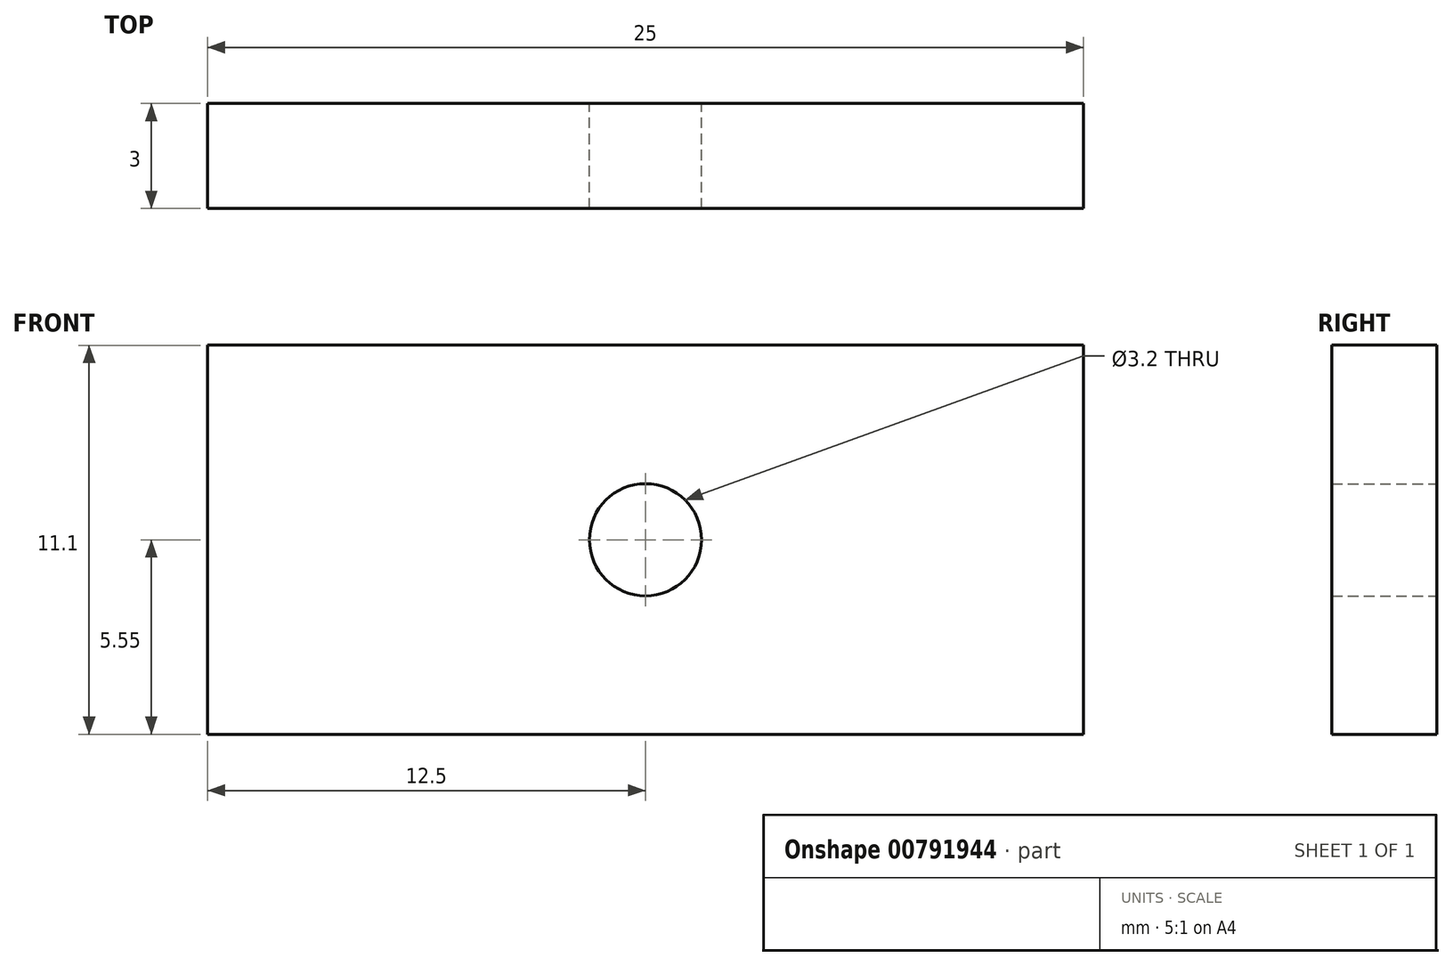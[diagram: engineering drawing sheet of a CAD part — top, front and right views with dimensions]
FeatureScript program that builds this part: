
annotation { "Feature Type Name" : "Feature", "Feature Type Description" : "" }
export const myFeature = defineFeature(function(context is Context, id is Id, definition is map)
    precondition{}
    {
        {
            var Q0;
            Q0=qCreatedBy(makeId("Front.planeOp"),FACE);
            var sketch = newSketch(context, id + "F0", { "sketchPlane" : qUnion([Q0])});
            skLineSegment(sketch, "E0.bottom", {"start": v(12.5, 5.56) * mm, "end": v(-12.5, 5.56) * mm});
            skLineSegment(sketch, "E0.top", {"start": v(12.5, -5.56) * mm, "end": v(-12.5, -5.56) * mm});
            skLineSegment(sketch, "E0.left", {"start": v(12.5, 5.56) * mm, "end": v(12.5, -5.56) * mm});
            skLineSegment(sketch, "E0.right", {"start": v(-12.5, 5.56) * mm, "end": v(-12.5, -5.56) * mm});
            skPoint(sketch, "E0.middle", {"position": v(0, 0) * mm});
            skCircle(sketch, "E1", {"center": v(0, 0) * mm, "radius": 1.6 * mm});
            skSolve(sketch);
        }
        {
            var Q0;
            Q0=makeQuery(id+"F0.imprint","IMPRINT",FACE,{"disambiguationData":[TD([[makeQuery(id+"F0.imprint","IMPRINT",EDGE,{"derivedFrom":sQuery(id+"F0.wireOp",EDGE,"E0.bottom")}),1.0]])]});
            extrude(context, id + "F1", {"entities" : qUnion([Q0]), "depth" : 3 * mm, "offsetDistance" : 25 * mm});
        }
    });
